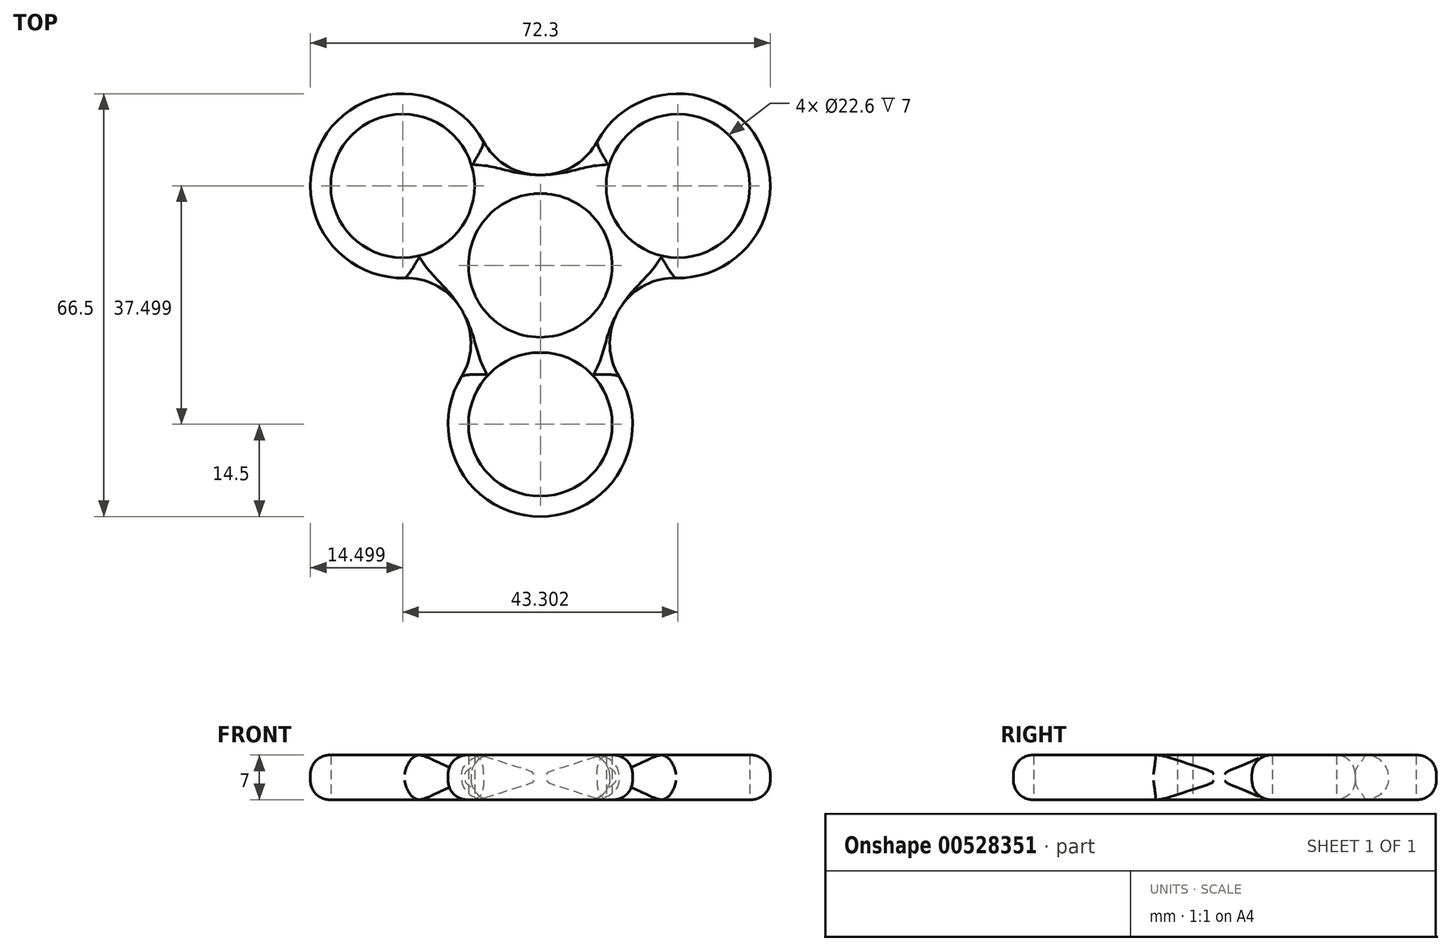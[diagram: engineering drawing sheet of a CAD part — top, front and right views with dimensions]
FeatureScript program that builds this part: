
annotation { "Feature Type Name" : "Feature", "Feature Type Description" : "" }
export const myFeature = defineFeature(function(context is Context, id is Id, definition is map)
    precondition{}
    {
        {
            var Q0;
            Q0=qCreatedBy(makeId("Top.planeOp"),FACE);
            var sketch = newSketch(context, id + "F0", { "sketchPlane" : qUnion([Q0])});
            skCircle(sketch, "E0", {"center": v(0, 0) * mm, "radius": 11.3 * mm});
            skCircle(sketch, "E1", {"center": v(0, 0) * mm, "radius": 25 * mm});
            skCircle(sketch, "E2", {"center": v(21.65, 12.5) * mm, "radius": 14.5 * mm});
            skCircle(sketch, "E3", {"center": v(-21.65, 12.5) * mm, "radius": 14.5 * mm});
            skCircle(sketch, "E4", {"center": v(0, -25) * mm, "radius": 14.5 * mm});
            skCircle(sketch, "E5", {"center": v(-21.65, 12.5) * mm, "radius": 11.3 * mm});
            skCircle(sketch, "E6", {"center": v(21.65, 12.5) * mm, "radius": 11.3 * mm});
            skCircle(sketch, "E7", {"center": v(0, -25) * mm, "radius": 11.3 * mm});
            skArc(sketch, "E8", {"start": v(-13.88, -20.8) * mm, "mid": v(-12.3, -7.1) * mm, "end": v(-24.95, -1.62) * mm});
            skArc(sketch, "E9", {"start": v(24.95, -1.62) * mm, "mid": v(12.3, -7.1) * mm, "end": v(13.88, -20.8) * mm});
            skArc(sketch, "E10", {"start": v(-11.07, 22.41) * mm, "mid": v(0, 14.21) * mm, "end": v(11.07, 22.41) * mm});
            skSolve(sketch);
        }
        {
            var Q0;
            {var subQ1=sQuery(id+"F0.wireOp",EDGE,"E1");var subQ3=sQuery(id+"F0.wireOp",EDGE,"E5");var subQ4=makeQuery(id+"F0.imprint","INTERSECT",VERTEX,{"disambiguationData":[OD(0.0)],"derivedFrom":[subQ1,subQ3]});Q0=makeQuery(id+"F0.imprint","IMPRINT",FACE,{"disambiguationData":[TD([[makeQuery(id+"F0.imprint","IMPRINT",EDGE,{"disambiguationData":[TD([[subQ4,-1.0]])],"derivedFrom":subQ3}),-1.0]])]});}
            var Q1;
            {var subQ0=sQuery(id+"F0.wireOp",EDGE,"E3");var subQ1=sQuery(id+"F0.wireOp",EDGE,"E0");var subQ2=makeQuery(id+"F0.imprint","INTERSECT",VERTEX,{"disambiguationData":[OD(1.0)],"derivedFrom":[subQ1,subQ0]});Q1=makeQuery(id+"F0.imprint","IMPRINT",FACE,{"disambiguationData":[TD([[makeQuery(id+"F0.imprint","IMPRINT",EDGE,{"disambiguationData":[TD([[subQ2,-1.0]])],"derivedFrom":subQ1}),-1.0]])]});}
            var Q2;
            {var subQ0=sQuery(id+"F0.wireOp",EDGE,"E4");var subQ1=sQuery(id+"F0.wireOp",EDGE,"E0");var subQ12=makeQuery(id+"F0.imprint","INTERSECT",VERTEX,{"disambiguationData":[OD(0.0)],"derivedFrom":[subQ1,subQ0]});Q2=makeQuery(id+"F0.imprint","IMPRINT",FACE,{"disambiguationData":[TD([[makeQuery(id+"F0.imprint","IMPRINT",EDGE,{"disambiguationData":[TD([[subQ12,-1.0]])],"derivedFrom":subQ1}),-1.0]])]});}
            var Q3;
            {var subQ0=sQuery(id+"F0.wireOp",EDGE,"E2");var subQ1=sQuery(id+"F0.wireOp",EDGE,"E0");var subQ2=makeQuery(id+"F0.imprint","INTERSECT",VERTEX,{"disambiguationData":[OD(1.0)],"derivedFrom":[subQ1,subQ0]});Q3=makeQuery(id+"F0.imprint","IMPRINT",FACE,{"disambiguationData":[TD([[makeQuery(id+"F0.imprint","IMPRINT",EDGE,{"disambiguationData":[TD([[subQ2,1.0]])],"derivedFrom":subQ1}),-1.0]])]});}
            var Q4;
            {var subQ0=sQuery(id+"F0.wireOp",EDGE,"E2");var subQ1=sQuery(id+"F0.wireOp",EDGE,"E0");var subQ2=makeQuery(id+"F0.imprint","INTERSECT",VERTEX,{"disambiguationData":[OD(0.0)],"derivedFrom":[subQ1,subQ0]});Q4=makeQuery(id+"F0.imprint","IMPRINT",FACE,{"disambiguationData":[TD([[makeQuery(id+"F0.imprint","IMPRINT",EDGE,{"disambiguationData":[TD([[subQ2,1.0]])],"derivedFrom":subQ1}),-1.0]])]});}
            var Q5;
            {var subQ0=sQuery(id+"F0.wireOp",EDGE,"E2");var subQ1=sQuery(id+"F0.wireOp",EDGE,"E0");var subQ2=makeQuery(id+"F0.imprint","INTERSECT",VERTEX,{"disambiguationData":[OD(0.0)],"derivedFrom":[subQ1,subQ0]});Q5=makeQuery(id+"F0.imprint","IMPRINT",FACE,{"disambiguationData":[TD([[makeQuery(id+"F0.imprint","IMPRINT",EDGE,{"disambiguationData":[TD([[subQ2,-1.0]])],"derivedFrom":subQ1}),-1.0]])]});}
            var Q6;
            {var subQ1=sQuery(id+"F0.wireOp",EDGE,"E1");var subQ3=sQuery(id+"F0.wireOp",EDGE,"E6");var subQ4=makeQuery(id+"F0.imprint","INTERSECT",VERTEX,{"disambiguationData":[OD(0.0)],"derivedFrom":[subQ1,subQ3]});Q6=makeQuery(id+"F0.imprint","IMPRINT",FACE,{"disambiguationData":[TD([[makeQuery(id+"F0.imprint","IMPRINT",EDGE,{"disambiguationData":[TD([[subQ4,1.0]])],"derivedFrom":subQ3}),-1.0]])]});}
            var Q7;
            {var subQ0=sQuery(id+"F0.wireOp",EDGE,"E10");var subQ1=sQuery(id+"F0.wireOp",EDGE,"E2");var subQ3=makeQuery(id+"F0.imprint","INTERSECT",VERTEX,{"derivedFrom":[subQ1,subQ0]});Q7=makeQuery(id+"F0.imprint","IMPRINT",FACE,{"disambiguationData":[TD([[makeQuery(id+"F0.imprint","IMPRINT",EDGE,{"disambiguationData":[TD([[subQ3,1.0]])],"derivedFrom":subQ1}),1.0]])]});}
            var Q8;
            {var subQ0=sQuery(id+"F0.wireOp",EDGE,"E10");var subQ1=sQuery(id+"F0.wireOp",EDGE,"E3");var subQ3=makeQuery(id+"F0.imprint","INTERSECT",VERTEX,{"derivedFrom":[subQ1,subQ0]});Q8=makeQuery(id+"F0.imprint","IMPRINT",FACE,{"disambiguationData":[TD([[makeQuery(id+"F0.imprint","IMPRINT",EDGE,{"disambiguationData":[TD([[subQ3,-1.0]])],"derivedFrom":subQ1}),1.0]])]});}
            var Q9;
            {var subQ1=sQuery(id+"F0.wireOp",EDGE,"E3");var subQ10=sQuery(id+"F0.wireOp",EDGE,"E0");var subQ12=makeQuery(id+"F0.imprint","INTERSECT",VERTEX,{"disambiguationData":[OD(0.0)],"derivedFrom":[subQ10,subQ1]});Q9=makeQuery(id+"F0.imprint","IMPRINT",FACE,{"disambiguationData":[TD([[makeQuery(id+"F0.imprint","IMPRINT",EDGE,{"disambiguationData":[TD([[subQ12,-1.0]])],"derivedFrom":subQ10}),-1.0]])]});}
            var Q10;
            {var subQ0=sQuery(id+"F0.wireOp",EDGE,"E8");var subQ1=sQuery(id+"F0.wireOp",EDGE,"E3");var subQ3=makeQuery(id+"F0.imprint","INTERSECT",VERTEX,{"derivedFrom":[subQ1,subQ0]});Q10=makeQuery(id+"F0.imprint","IMPRINT",FACE,{"disambiguationData":[TD([[makeQuery(id+"F0.imprint","IMPRINT",EDGE,{"disambiguationData":[TD([[subQ3,1.0]])],"derivedFrom":subQ1}),1.0]])]});}
            var Q11;
            {var subQ0=sQuery(id+"F0.wireOp",EDGE,"E8");var subQ1=sQuery(id+"F0.wireOp",EDGE,"E4");var subQ3=makeQuery(id+"F0.imprint","INTERSECT",VERTEX,{"derivedFrom":[subQ1,subQ0]});Q11=makeQuery(id+"F0.imprint","IMPRINT",FACE,{"disambiguationData":[TD([[makeQuery(id+"F0.imprint","IMPRINT",EDGE,{"disambiguationData":[TD([[subQ3,-1.0]])],"derivedFrom":subQ1}),1.0]])]});}
            var Q12;
            {var subQ0=sQuery(id+"F0.wireOp",EDGE,"E9");var subQ1=sQuery(id+"F0.wireOp",EDGE,"E4");var subQ3=makeQuery(id+"F0.imprint","INTERSECT",VERTEX,{"derivedFrom":[subQ1,subQ0]});Q12=makeQuery(id+"F0.imprint","IMPRINT",FACE,{"disambiguationData":[TD([[makeQuery(id+"F0.imprint","IMPRINT",EDGE,{"disambiguationData":[TD([[subQ3,1.0]])],"derivedFrom":subQ1}),1.0]])]});}
            var Q13;
            {var subQ0=sQuery(id+"F0.wireOp",EDGE,"E9");var subQ1=sQuery(id+"F0.wireOp",EDGE,"E2");var subQ3=makeQuery(id+"F0.imprint","INTERSECT",VERTEX,{"derivedFrom":[subQ1,subQ0]});Q13=makeQuery(id+"F0.imprint","IMPRINT",FACE,{"disambiguationData":[TD([[makeQuery(id+"F0.imprint","IMPRINT",EDGE,{"disambiguationData":[TD([[subQ3,-1.0]])],"derivedFrom":subQ1}),1.0]])]});}
            var Q14;
            {var subQ1=sQuery(id+"F0.wireOp",EDGE,"E1");var subQ3=sQuery(id+"F0.wireOp",EDGE,"E7");var subQ4=makeQuery(id+"F0.imprint","INTERSECT",VERTEX,{"disambiguationData":[OD(0.0)],"derivedFrom":[subQ1,subQ3]});Q14=makeQuery(id+"F0.imprint","IMPRINT",FACE,{"disambiguationData":[TD([[makeQuery(id+"F0.imprint","IMPRINT",EDGE,{"disambiguationData":[TD([[subQ4,-1.0]])],"derivedFrom":subQ3}),-1.0]])]});}
            extrude(context, id + "F1", {"entities" : qUnion([Q0, Q1, Q2, Q3, Q4, Q5, Q6, Q7, Q8, Q9, Q10, Q11, Q12, Q13, Q14]), "depth" : 7 * mm, "offsetDistance" : 25 * mm});
        }
        {
            var Q0;
            Q0=makeQuery(id+"F1.opExtrude","CAP_EDGE",EDGE,{"disambiguationData":[OSD([sQuery(id+"F0.wireOp",EDGE,"E3")])],"isStart":false});
            var Q1;
            Q1=makeQuery(id+"F1.opExtrude","CAP_EDGE",EDGE,{"disambiguationData":[OSD([sQuery(id+"F0.wireOp",EDGE,"E10")])],"isStart":false});
            var Q2;
            Q2=makeQuery(id+"F1.opExtrude","CAP_EDGE",EDGE,{"disambiguationData":[OSD([sQuery(id+"F0.wireOp",EDGE,"E2")])],"isStart":false});
            var Q3;
            Q3=makeQuery(id+"F1.opExtrude","CAP_EDGE",EDGE,{"disambiguationData":[OSD([sQuery(id+"F0.wireOp",EDGE,"E9")])],"isStart":false});
            var Q4;
            Q4=makeQuery(id+"F1.opExtrude","CAP_EDGE",EDGE,{"disambiguationData":[OSD([sQuery(id+"F0.wireOp",EDGE,"E4")])],"isStart":false});
            var Q5;
            Q5=makeQuery(id+"F1.opExtrude","CAP_EDGE",EDGE,{"disambiguationData":[OSD([sQuery(id+"F0.wireOp",EDGE,"E8")])],"isStart":false});
            fillet(context, id + "F2", {"entities" : qUnion([Q0, Q1, Q2, Q3, Q4, Q5]), "radius" : 3 * mm, "tangentPropagation" : true, "allowEdgeOverflow" : false});
        }
        {
            var Q0;
            Q0=makeQuery(id+"F1.opExtrude","CAP_EDGE",EDGE,{"disambiguationData":[OSD([sQuery(id+"F0.wireOp",EDGE,"E3")])],"isStart":true});
            var Q1;
            Q1=makeQuery(id+"F1.opExtrude","CAP_EDGE",EDGE,{"disambiguationData":[OSD([sQuery(id+"F0.wireOp",EDGE,"E10")])],"isStart":true});
            var Q2;
            Q2=makeQuery(id+"F1.opExtrude","CAP_EDGE",EDGE,{"disambiguationData":[OSD([sQuery(id+"F0.wireOp",EDGE,"E2")])],"isStart":true});
            var Q3;
            Q3=makeQuery(id+"F1.opExtrude","CAP_EDGE",EDGE,{"disambiguationData":[OSD([sQuery(id+"F0.wireOp",EDGE,"E9")])],"isStart":true});
            var Q4;
            Q4=makeQuery(id+"F1.opExtrude","CAP_EDGE",EDGE,{"disambiguationData":[OSD([sQuery(id+"F0.wireOp",EDGE,"E8")])],"isStart":true});
            var Q5;
            Q5=makeQuery(id+"F1.opExtrude","CAP_EDGE",EDGE,{"disambiguationData":[OSD([sQuery(id+"F0.wireOp",EDGE,"E4")])],"isStart":true});
            fillet(context, id + "F3", {"entities" : qUnion([Q0, Q1, Q2, Q3, Q4, Q5]), "radius" : 3 * mm, "tangentPropagation" : true, "allowEdgeOverflow" : false});
        }
        {
            var Q0;
            Q0=makeQuery(id+"F3.opFillet","BLEND_EDGE",EDGE,{"blendedFrom":[makeQuery(id+"F1.opExtrude","CAP_EDGE",EDGE,{"disambiguationData":[OSD([sQuery(id+"F0.wireOp",EDGE,"E3")])],"isStart":true}),makeQuery(id+"F1.opExtrude","CAP_EDGE",EDGE,{"disambiguationData":[OSD([sQuery(id+"F0.wireOp",EDGE,"E8")])],"isStart":true})],"blendedInto":[]});
            var Q1;
            Q1=makeQuery(id+"F1.opExtrude","SWEPT_EDGE",EDGE,{"disambiguationData":[OSD([sQuery(id+"F0.wireOp",EDGE,"E3"),sQuery(id+"F0.wireOp",EDGE,"E8")])]});
            var Q2;
            Q2=makeQuery(id+"F2.opFillet","BLEND_EDGE",EDGE,{"blendedFrom":[makeQuery(id+"F1.opExtrude","CAP_EDGE",EDGE,{"disambiguationData":[OSD([sQuery(id+"F0.wireOp",EDGE,"E3")])],"isStart":false}),makeQuery(id+"F1.opExtrude","CAP_EDGE",EDGE,{"disambiguationData":[OSD([sQuery(id+"F0.wireOp",EDGE,"E8")])],"isStart":false})],"blendedInto":[]});
            var Q3;
            Q3=makeQuery(id+"F3.opFillet","BLEND_EDGE",EDGE,{"blendedFrom":[makeQuery(id+"F1.opExtrude","CAP_EDGE",EDGE,{"disambiguationData":[OSD([sQuery(id+"F0.wireOp",EDGE,"E4")])],"isStart":true}),makeQuery(id+"F1.opExtrude","CAP_EDGE",EDGE,{"disambiguationData":[OSD([sQuery(id+"F0.wireOp",EDGE,"E8")])],"isStart":true})],"blendedInto":[]});
            var Q4;
            Q4=makeQuery(id+"F1.opExtrude","SWEPT_EDGE",EDGE,{"disambiguationData":[OSD([sQuery(id+"F0.wireOp",EDGE,"E4"),sQuery(id+"F0.wireOp",EDGE,"E8")])]});
            var Q5;
            Q5=makeQuery(id+"F2.opFillet","BLEND_EDGE",EDGE,{"blendedFrom":[makeQuery(id+"F1.opExtrude","CAP_EDGE",EDGE,{"disambiguationData":[OSD([sQuery(id+"F0.wireOp",EDGE,"E4")])],"isStart":false}),makeQuery(id+"F1.opExtrude","CAP_EDGE",EDGE,{"disambiguationData":[OSD([sQuery(id+"F0.wireOp",EDGE,"E8")])],"isStart":false})],"blendedInto":[]});
            var Q6;
            Q6=makeQuery(id+"F2.opFillet","BLEND_EDGE",EDGE,{"blendedFrom":[makeQuery(id+"F1.opExtrude","CAP_EDGE",EDGE,{"disambiguationData":[OSD([sQuery(id+"F0.wireOp",EDGE,"E3")])],"isStart":false}),makeQuery(id+"F1.opExtrude","CAP_EDGE",EDGE,{"disambiguationData":[OSD([sQuery(id+"F0.wireOp",EDGE,"E10")])],"isStart":false})],"blendedInto":[]});
            var Q7;
            Q7=makeQuery(id+"F1.opExtrude","SWEPT_EDGE",EDGE,{"disambiguationData":[OSD([sQuery(id+"F0.wireOp",EDGE,"E3"),sQuery(id+"F0.wireOp",EDGE,"E10")])]});
            var Q8;
            Q8=makeQuery(id+"F3.opFillet","BLEND_EDGE",EDGE,{"blendedFrom":[makeQuery(id+"F1.opExtrude","CAP_EDGE",EDGE,{"disambiguationData":[OSD([sQuery(id+"F0.wireOp",EDGE,"E3")])],"isStart":true}),makeQuery(id+"F1.opExtrude","CAP_EDGE",EDGE,{"disambiguationData":[OSD([sQuery(id+"F0.wireOp",EDGE,"E10")])],"isStart":true})],"blendedInto":[]});
            var Q9;
            Q9=makeQuery(id+"F3.opFillet","BLEND_EDGE",EDGE,{"blendedFrom":[makeQuery(id+"F1.opExtrude","CAP_EDGE",EDGE,{"disambiguationData":[OSD([sQuery(id+"F0.wireOp",EDGE,"E2")])],"isStart":true}),makeQuery(id+"F1.opExtrude","CAP_EDGE",EDGE,{"disambiguationData":[OSD([sQuery(id+"F0.wireOp",EDGE,"E10")])],"isStart":true})],"blendedInto":[]});
            var Q10;
            Q10=makeQuery(id+"F1.opExtrude","SWEPT_EDGE",EDGE,{"disambiguationData":[OSD([sQuery(id+"F0.wireOp",EDGE,"E2"),sQuery(id+"F0.wireOp",EDGE,"E10")])]});
            var Q11;
            Q11=makeQuery(id+"F2.opFillet","BLEND_EDGE",EDGE,{"blendedFrom":[makeQuery(id+"F1.opExtrude","CAP_EDGE",EDGE,{"disambiguationData":[OSD([sQuery(id+"F0.wireOp",EDGE,"E2")])],"isStart":false}),makeQuery(id+"F1.opExtrude","CAP_EDGE",EDGE,{"disambiguationData":[OSD([sQuery(id+"F0.wireOp",EDGE,"E10")])],"isStart":false})],"blendedInto":[]});
            var Q12;
            Q12=makeQuery(id+"F1.opExtrude","SWEPT_EDGE",EDGE,{"disambiguationData":[OSD([sQuery(id+"F0.wireOp",EDGE,"E2"),sQuery(id+"F0.wireOp",EDGE,"E9")])]});
            var Q13;
            Q13=makeQuery(id+"F2.opFillet","BLEND_EDGE",EDGE,{"blendedFrom":[makeQuery(id+"F1.opExtrude","CAP_EDGE",EDGE,{"disambiguationData":[OSD([sQuery(id+"F0.wireOp",EDGE,"E2")])],"isStart":false}),makeQuery(id+"F1.opExtrude","CAP_EDGE",EDGE,{"disambiguationData":[OSD([sQuery(id+"F0.wireOp",EDGE,"E9")])],"isStart":false})],"blendedInto":[]});
            var Q14;
            Q14=makeQuery(id+"F3.opFillet","BLEND_EDGE",EDGE,{"blendedFrom":[makeQuery(id+"F1.opExtrude","CAP_EDGE",EDGE,{"disambiguationData":[OSD([sQuery(id+"F0.wireOp",EDGE,"E2")])],"isStart":true}),makeQuery(id+"F1.opExtrude","CAP_EDGE",EDGE,{"disambiguationData":[OSD([sQuery(id+"F0.wireOp",EDGE,"E9")])],"isStart":true})],"blendedInto":[]});
            var Q15;
            Q15=makeQuery(id+"F2.opFillet","BLEND_EDGE",EDGE,{"blendedFrom":[makeQuery(id+"F1.opExtrude","CAP_EDGE",EDGE,{"disambiguationData":[OSD([sQuery(id+"F0.wireOp",EDGE,"E4")])],"isStart":false}),makeQuery(id+"F1.opExtrude","CAP_EDGE",EDGE,{"disambiguationData":[OSD([sQuery(id+"F0.wireOp",EDGE,"E9")])],"isStart":false})],"blendedInto":[]});
            var Q16;
            Q16=makeQuery(id+"F1.opExtrude","SWEPT_EDGE",EDGE,{"disambiguationData":[OSD([sQuery(id+"F0.wireOp",EDGE,"E4"),sQuery(id+"F0.wireOp",EDGE,"E9")])]});
            var Q17;
            Q17=makeQuery(id+"F3.opFillet","BLEND_EDGE",EDGE,{"blendedFrom":[makeQuery(id+"F1.opExtrude","CAP_EDGE",EDGE,{"disambiguationData":[OSD([sQuery(id+"F0.wireOp",EDGE,"E4")])],"isStart":true}),makeQuery(id+"F1.opExtrude","CAP_EDGE",EDGE,{"disambiguationData":[OSD([sQuery(id+"F0.wireOp",EDGE,"E9")])],"isStart":true})],"blendedInto":[]});
            fillet(context, id + "F4", {"entities" : qUnion([Q0, Q1, Q2, Q3, Q4, Q5, Q6, Q7, Q8, Q9, Q10, Q11, Q12, Q13, Q14, Q15, Q16, Q17]), "radius" : 10 * mm, "tangentPropagation" : true, "allowEdgeOverflow" : false});
        }
    });
